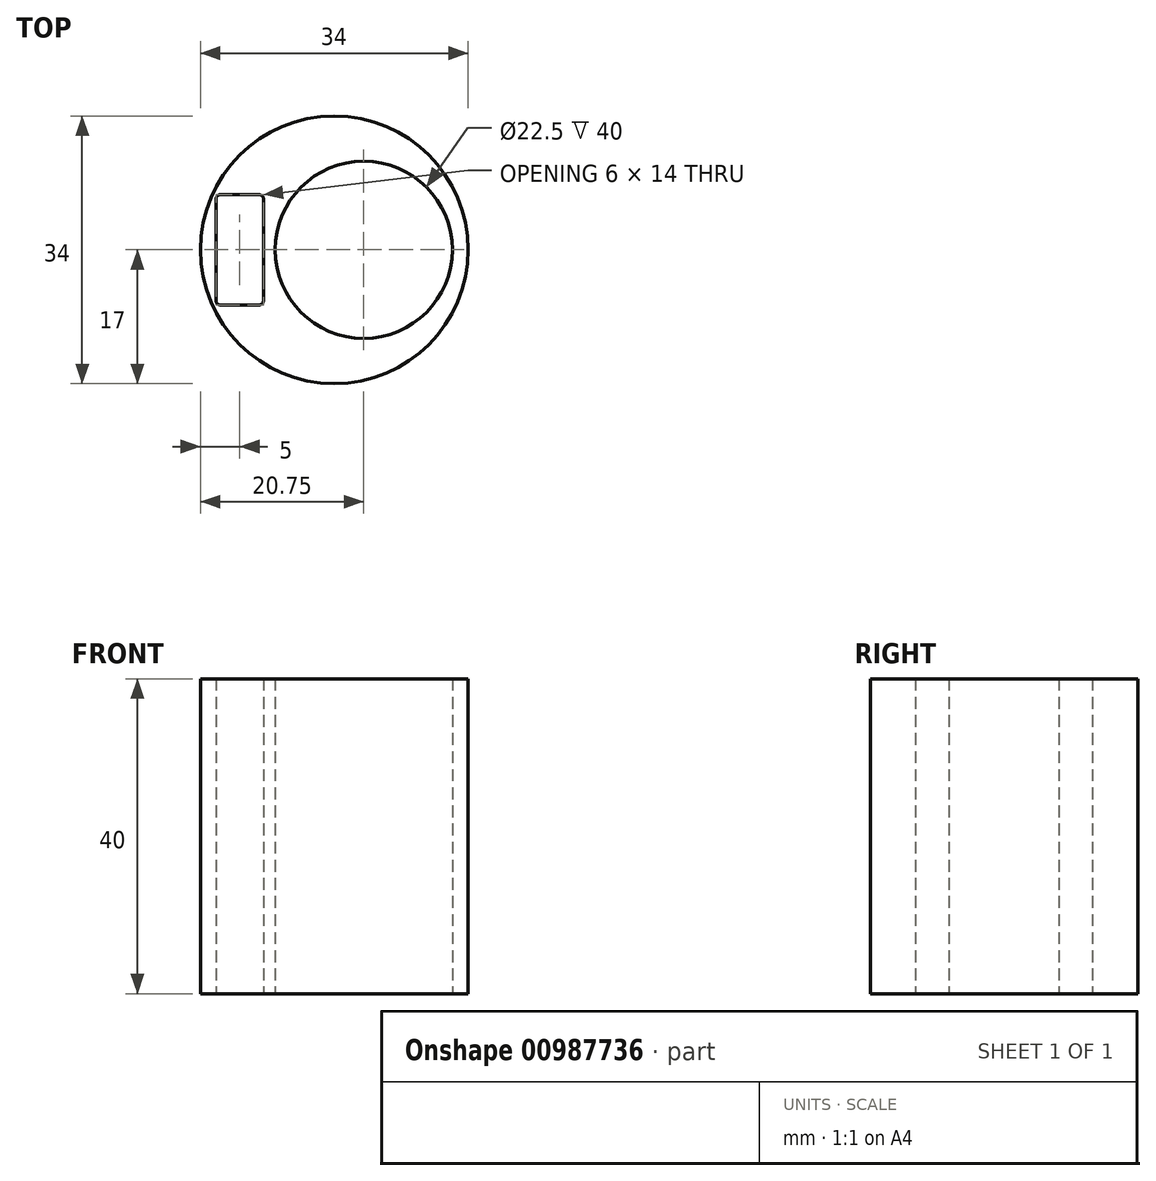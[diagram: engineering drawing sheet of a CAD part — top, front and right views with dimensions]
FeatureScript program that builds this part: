
annotation { "Feature Type Name" : "Feature", "Feature Type Description" : "" }
export const myFeature = defineFeature(function(context is Context, id is Id, definition is map)
    precondition{}
    {
        {
            var Q0;
            Q0=qCreatedBy(makeId("Top.planeOp"),FACE);
            var sketch = newSketch(context, id + "F0", { "sketchPlane" : qUnion([Q0])});
            skCircle(sketch, "E0", {"center": v(0, 0) * mm, "radius": 21 * mm});
            skCircle(sketch, "E1", {"center": v(0, 0) * mm, "radius": 17 * mm});
            skCircle(sketch, "E2", {"center": v(3.75, 0) * mm, "radius": 11.25 * mm});
            skLineSegment(sketch, "E3.bottom", {"start": v(-9.5, -7) * mm, "end": v(-14.5, -7) * mm});
            skLineSegment(sketch, "E3.top", {"start": v(-9.5, 7) * mm, "end": v(-14.5, 7) * mm});
            skLineSegment(sketch, "E3.left", {"start": v(-9, -6.5) * mm, "end": v(-9, 6.5) * mm});
            skLineSegment(sketch, "E3.right", {"start": v(-15, -6.5) * mm, "end": v(-15, 6.5) * mm});
            skPoint(sketch, "E3.middle", {"position": v(-12, 0) * mm});
            skPoint(sketch, "E4.visualSharp", {"position": v(-15, 7) * mm});
            skArc(sketch, "E4.filletArc", {"start": v(-14.5, 7) * mm, "mid": v(-14.85, 6.85) * mm, "end": v(-15, 6.5) * mm});
            skPoint(sketch, "E5.visualSharp", {"position": v(-9, 7) * mm});
            skArc(sketch, "E5.filletArc", {"start": v(-9, 6.5) * mm, "mid": v(-9.15, 6.85) * mm, "end": v(-9.5, 7) * mm});
            skPoint(sketch, "E6.visualSharp", {"position": v(-9, -7) * mm});
            skArc(sketch, "E6.filletArc", {"start": v(-9.5, -7) * mm, "mid": v(-9.15, -6.85) * mm, "end": v(-9, -6.5) * mm});
            skPoint(sketch, "E7.visualSharp", {"position": v(-15, -7) * mm});
            skArc(sketch, "E7.filletArc", {"start": v(-15, -6.5) * mm, "mid": v(-14.85, -6.85) * mm, "end": v(-14.5, -7) * mm});
            skSolve(sketch);
        }
        {
            var Q0;
            Q0=makeQuery(id+"F0.imprint","IMPRINT",FACE,{"disambiguationData":[TD([[makeQuery(id+"F0.imprint","IMPRINT",EDGE,{"derivedFrom":sQuery(id+"F0.wireOp",EDGE,"E1")}),1.0]])]});
            extrude(context, id + "F1", {"entities" : qUnion([Q0]), "depth" : 40 * mm, "offsetDistance" : 25 * mm});
        }
    });
